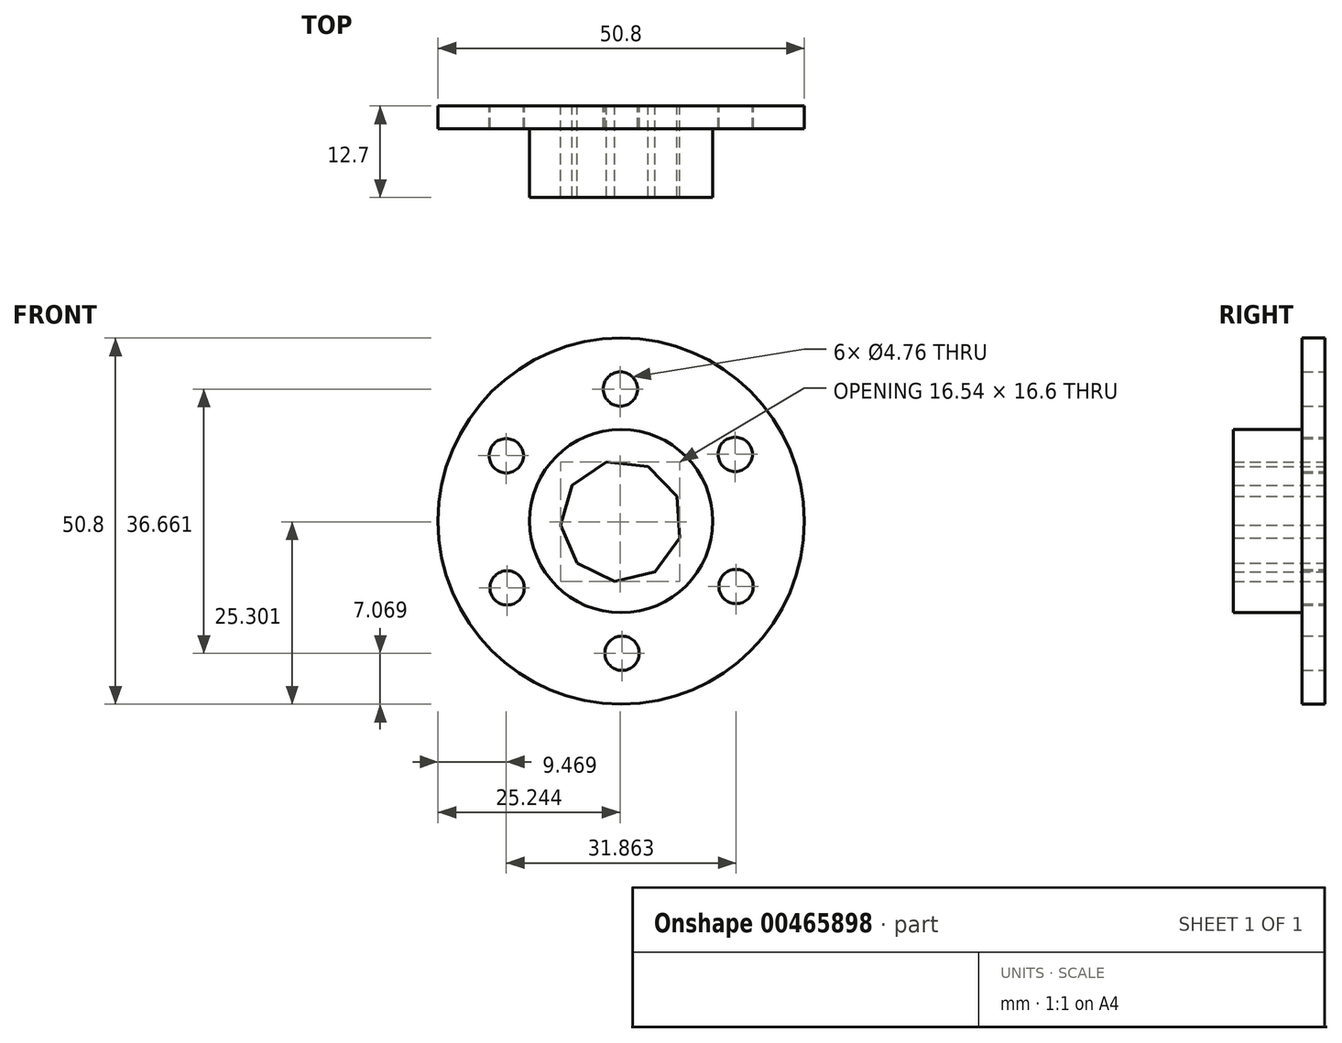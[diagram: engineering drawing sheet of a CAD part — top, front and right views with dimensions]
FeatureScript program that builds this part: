
annotation { "Feature Type Name" : "Feature", "Feature Type Description" : "" }
export const myFeature = defineFeature(function(context is Context, id is Id, definition is map)
    precondition{}
    {
        {
            var Q0;
            Q0=qCreatedBy(makeId("Front.planeOp"),FACE);
            var sketch = newSketch(context, id + "F0", { "sketchPlane" : qUnion([Q0])});
            skCircle(sketch, "E0", {"center": v(0, 0) * mm, "radius": 25.4 * mm});
            skCircle(sketch, "E1", {"center": v(0, 0) * mm, "radius": 12.7 * mm});
            skCircle(sketch, "E2", {"center": v(0, 0) * mm, "radius": 7.94 * mm});
            skSolve(sketch);
        }
        {
            var Q0;
            Q0=makeQuery(id+"F0.imprint","IMPRINT",FACE,{"disambiguationData":[TD([[makeQuery(id+"F0.imprint","IMPRINT",EDGE,{"derivedFrom":sQuery(id+"F0.wireOp",EDGE,"E0")}),1.0]])]});
            extrude(context, id + "F1", {"entities" : qUnion([Q0]), "depth" : 3.17 * mm});
        }
        {
            var Q0;
            Q0=qCreatedBy(makeId("Front.planeOp"),FACE);
            var sketch = newSketch(context, id + "F2", { "sketchPlane" : qUnion([Q0])});
            skCircle(sketch, "E3", {"center": v(0, 0) * mm, "radius": 12.7 * mm});
            skSolve(sketch);
        }
        {
            var Q0;
            Q0=makeQuery(id+"F2.imprint","IMPRINT",FACE,{"disambiguationData":[TD([[makeQuery(id+"F2.imprint","IMPRINT",EDGE,{"derivedFrom":sQuery(id+"F2.wireOp",EDGE,"E3")}),1.0]])]});
            extrude(context, id + "F3", {"entities" : qUnion([Q0]), "operationType" : NewBodyOperationType.ADD, "depth" : 12.7 * mm});
        }
        {
            var Q0;
            Q0=qCreatedBy(makeId("Front.planeOp"),FACE);
            var sketch = newSketch(context, id + "F4", { "sketchPlane" : qUnion([Q0])});
            skCircle(sketch, "E4", {"center": v(0, 0) * mm, "radius": 7.94 * mm});
            skSolve(sketch);
        }
        {
            var Q0;
            Q0 = qSketchRegion(id + "F4", true);
            extrude(context, id + "F5", {"entities" : qUnion([Q0]), "operationType" : NewBodyOperationType.REMOVE, "oppositeDirection" : true, "depth" : -76.2 * mm});
        }
        {
            var Q0;
            Q0=qCreatedBy(makeId("Front.planeOp"),FACE);
            var sketch = newSketch(context, id + "F6", { "sketchPlane" : qUnion([Q0])});
            skCircle(sketch, "E5", {"center": v(0, 0) * mm, "radius": 15.88 * mm});
            skCircle(sketch, "E6.cCircle", {"center": v(0, 0) * mm, "radius": 15.88 * mm, "construction": true});
            skLineSegment(sketch, "E6.0", {"start": v(-15.93, 9.07) * mm, "end": v(-0.11, 18.33) * mm});
            skLineSegment(sketch, "E6.1", {"start": v(-0.11, 18.33) * mm, "end": v(15.82, 9.26) * mm});
            skLineSegment(sketch, "E6.2", {"start": v(15.82, 9.26) * mm, "end": v(15.93, -9.07) * mm});
            skLineSegment(sketch, "E6.3", {"start": v(15.93, -9.07) * mm, "end": v(0.11, -18.33) * mm});
            skLineSegment(sketch, "E6.4", {"start": v(0.11, -18.33) * mm, "end": v(-15.82, -9.26) * mm});
            skLineSegment(sketch, "E6.5", {"start": v(-15.82, -9.26) * mm, "end": v(-15.93, 9.07) * mm});
            skPoint(sketch, "E6.0.midPoint", {"position": v(-8.02, 13.7) * mm});
            skCircle(sketch, "E7", {"center": v(-0.11, 18.33) * mm, "radius": 2.38 * mm});
            skCircle(sketch, "E8", {"center": v(-15.93, 9.07) * mm, "radius": 2.38 * mm});
            skCircle(sketch, "E9", {"center": v(-15.82, -9.26) * mm, "radius": 2.38 * mm});
            skCircle(sketch, "E10", {"center": v(0.11, -18.33) * mm, "radius": 2.38 * mm});
            skCircle(sketch, "E11", {"center": v(15.93, -9.07) * mm, "radius": 2.38 * mm});
            skCircle(sketch, "E12", {"center": v(15.82, 9.26) * mm, "radius": 2.38 * mm});
            skSolve(sketch);
        }
        {
            var Q0;
            {var subQ0=sQuery(id+"F6.wireOp",EDGE,"E6.1");var subQ1=sQuery(id+"F6.wireOp",EDGE,"E6.0");var subQ2=makeQuery(id+"F6.imprint","INTERSECT",VERTEX,{"derivedFrom":[subQ1,subQ0]});Q0=makeQuery(id+"F6.imprint","IMPRINT",FACE,{"disambiguationData":[TD([[makeQuery(id+"F6.imprint","IMPRINT",EDGE,{"disambiguationData":[TD([[subQ2,1.0]])],"derivedFrom":subQ1}),1.0]])]});}
            var Q1;
            {var subQ0=sQuery(id+"F6.wireOp",EDGE,"E6.1");var subQ1=sQuery(id+"F6.wireOp",EDGE,"E6.0");var subQ2=makeQuery(id+"F6.imprint","INTERSECT",VERTEX,{"derivedFrom":[subQ1,subQ0]});Q1=makeQuery(id+"F6.imprint","IMPRINT",FACE,{"disambiguationData":[TD([[makeQuery(id+"F6.imprint","IMPRINT",EDGE,{"disambiguationData":[TD([[subQ2,1.0]])],"derivedFrom":subQ1}),-1.0]])]});}
            var Q2;
            {var subQ0=sQuery(id+"F6.wireOp",EDGE,"E6.5");var subQ1=sQuery(id+"F6.wireOp",EDGE,"E6.0");var subQ2=makeQuery(id+"F6.imprint","INTERSECT",VERTEX,{"derivedFrom":[subQ1,subQ0]});Q2=makeQuery(id+"F6.imprint","IMPRINT",FACE,{"disambiguationData":[TD([[makeQuery(id+"F6.imprint","IMPRINT",EDGE,{"disambiguationData":[TD([[subQ2,-1.0]])],"derivedFrom":subQ1}),1.0]])]});}
            var Q3;
            {var subQ0=sQuery(id+"F6.wireOp",EDGE,"E6.5");var subQ1=sQuery(id+"F6.wireOp",EDGE,"E6.0");var subQ2=makeQuery(id+"F6.imprint","INTERSECT",VERTEX,{"derivedFrom":[subQ1,subQ0]});Q3=makeQuery(id+"F6.imprint","IMPRINT",FACE,{"disambiguationData":[TD([[makeQuery(id+"F6.imprint","IMPRINT",EDGE,{"disambiguationData":[TD([[subQ2,-1.0]])],"derivedFrom":subQ1}),-1.0]])]});}
            var Q4;
            {var subQ0=sQuery(id+"F6.wireOp",EDGE,"E6.2");var subQ1=sQuery(id+"F6.wireOp",EDGE,"E6.1");var subQ2=makeQuery(id+"F6.imprint","INTERSECT",VERTEX,{"derivedFrom":[subQ1,subQ0]});Q4=makeQuery(id+"F6.imprint","IMPRINT",FACE,{"disambiguationData":[TD([[makeQuery(id+"F6.imprint","IMPRINT",EDGE,{"disambiguationData":[TD([[subQ2,1.0]])],"derivedFrom":subQ1}),1.0]])]});}
            var Q5;
            {var subQ0=sQuery(id+"F6.wireOp",EDGE,"E6.2");var subQ1=sQuery(id+"F6.wireOp",EDGE,"E6.1");var subQ2=makeQuery(id+"F6.imprint","INTERSECT",VERTEX,{"derivedFrom":[subQ1,subQ0]});Q5=makeQuery(id+"F6.imprint","IMPRINT",FACE,{"disambiguationData":[TD([[makeQuery(id+"F6.imprint","IMPRINT",EDGE,{"disambiguationData":[TD([[subQ2,1.0]])],"derivedFrom":subQ1}),-1.0]])]});}
            var Q6;
            {var subQ0=sQuery(id+"F6.wireOp",EDGE,"E6.3");var subQ1=sQuery(id+"F6.wireOp",EDGE,"E6.2");var subQ2=makeQuery(id+"F6.imprint","INTERSECT",VERTEX,{"derivedFrom":[subQ1,subQ0]});Q6=makeQuery(id+"F6.imprint","IMPRINT",FACE,{"disambiguationData":[TD([[makeQuery(id+"F6.imprint","IMPRINT",EDGE,{"disambiguationData":[TD([[subQ2,1.0]])],"derivedFrom":subQ1}),1.0]])]});}
            var Q7;
            {var subQ0=sQuery(id+"F6.wireOp",EDGE,"E6.3");var subQ1=sQuery(id+"F6.wireOp",EDGE,"E6.2");var subQ2=makeQuery(id+"F6.imprint","INTERSECT",VERTEX,{"derivedFrom":[subQ1,subQ0]});Q7=makeQuery(id+"F6.imprint","IMPRINT",FACE,{"disambiguationData":[TD([[makeQuery(id+"F6.imprint","IMPRINT",EDGE,{"disambiguationData":[TD([[subQ2,1.0]])],"derivedFrom":subQ1}),-1.0]])]});}
            var Q8;
            {var subQ0=sQuery(id+"F6.wireOp",EDGE,"E6.4");var subQ1=sQuery(id+"F6.wireOp",EDGE,"E6.3");var subQ2=makeQuery(id+"F6.imprint","INTERSECT",VERTEX,{"derivedFrom":[subQ1,subQ0]});Q8=makeQuery(id+"F6.imprint","IMPRINT",FACE,{"disambiguationData":[TD([[makeQuery(id+"F6.imprint","IMPRINT",EDGE,{"disambiguationData":[TD([[subQ2,1.0]])],"derivedFrom":subQ1}),1.0]])]});}
            var Q9;
            {var subQ0=sQuery(id+"F6.wireOp",EDGE,"E6.4");var subQ1=sQuery(id+"F6.wireOp",EDGE,"E6.3");var subQ2=makeQuery(id+"F6.imprint","INTERSECT",VERTEX,{"derivedFrom":[subQ1,subQ0]});Q9=makeQuery(id+"F6.imprint","IMPRINT",FACE,{"disambiguationData":[TD([[makeQuery(id+"F6.imprint","IMPRINT",EDGE,{"disambiguationData":[TD([[subQ2,1.0]])],"derivedFrom":subQ1}),-1.0]])]});}
            var Q10;
            {var subQ0=sQuery(id+"F6.wireOp",EDGE,"E6.5");var subQ1=sQuery(id+"F6.wireOp",EDGE,"E6.4");var subQ2=makeQuery(id+"F6.imprint","INTERSECT",VERTEX,{"derivedFrom":[subQ1,subQ0]});Q10=makeQuery(id+"F6.imprint","IMPRINT",FACE,{"disambiguationData":[TD([[makeQuery(id+"F6.imprint","IMPRINT",EDGE,{"disambiguationData":[TD([[subQ2,1.0]])],"derivedFrom":subQ1}),1.0]])]});}
            var Q11;
            {var subQ0=sQuery(id+"F6.wireOp",EDGE,"E6.5");var subQ1=sQuery(id+"F6.wireOp",EDGE,"E6.4");var subQ2=makeQuery(id+"F6.imprint","INTERSECT",VERTEX,{"derivedFrom":[subQ1,subQ0]});Q11=makeQuery(id+"F6.imprint","IMPRINT",FACE,{"disambiguationData":[TD([[makeQuery(id+"F6.imprint","IMPRINT",EDGE,{"disambiguationData":[TD([[subQ2,1.0]])],"derivedFrom":subQ1}),-1.0]])]});}
            extrude(context, id + "F7", {"entities" : qUnion([Q0, Q1, Q2, Q3, Q4, Q5, Q6, Q7, Q8, Q9, Q10, Q11]), "operationType" : NewBodyOperationType.REMOVE, "oppositeDirection" : true, "depth" : -25.4 * mm});
        }
        {
            var Q0;
            Q0=qCreatedBy(makeId("Front.planeOp"),FACE);
            var sketch = newSketch(context, id + "F8", { "sketchPlane" : qUnion([Q0])});
            skCircle(sketch, "E13", {"center": v(0, 0) * mm, "radius": 7.94 * mm});
            skCircle(sketch, "E14.cCircle", {"center": v(0, 0) * mm, "radius": 7.94 * mm, "construction": true});
            skLineSegment(sketch, "E14.0", {"start": v(-6.82, 4.98) * mm, "end": v(-2.03, 8.2) * mm});
            skLineSegment(sketch, "E14.1", {"start": v(-2.03, 8.2) * mm, "end": v(3.72, 7.58) * mm});
            skLineSegment(sketch, "E14.2", {"start": v(3.72, 7.58) * mm, "end": v(7.72, 3.42) * mm});
            skLineSegment(sketch, "E14.3", {"start": v(7.72, 3.42) * mm, "end": v(8.11, -2.34) * mm});
            skLineSegment(sketch, "E14.4", {"start": v(8.11, -2.34) * mm, "end": v(4.7, -7.01) * mm});
            skLineSegment(sketch, "E14.5", {"start": v(4.7, -7.01) * mm, "end": v(-0.9, -8.4) * mm});
            skLineSegment(sketch, "E14.6", {"start": v(-0.9, -8.4) * mm, "end": v(-6.09, -5.86) * mm});
            skLineSegment(sketch, "E14.7", {"start": v(-6.09, -5.86) * mm, "end": v(-8.43, -0.57) * mm});
            skLineSegment(sketch, "E14.8", {"start": v(-8.43, -0.57) * mm, "end": v(-6.82, 4.98) * mm});
            skPoint(sketch, "E14.0.midPoint", {"position": v(-4.43, 6.59) * mm});
            skSolve(sketch);
        }
        {
            var Q0;
            {var subQ0=sQuery(id+"F8.wireOp",EDGE,"E14.1");var subQ1=sQuery(id+"F8.wireOp",EDGE,"E13");var subQ2=makeQuery(id+"F8.imprint","INTERSECT",VERTEX,{"derivedFrom":[subQ1,subQ0]});Q0=makeQuery(id+"F8.imprint","IMPRINT",FACE,{"disambiguationData":[TD([[makeQuery(id+"F8.imprint","IMPRINT",EDGE,{"disambiguationData":[TD([[subQ2,-1.0]])],"derivedFrom":subQ1}),-1.0]])]});}
            var Q1;
            {var subQ0=sQuery(id+"F8.wireOp",EDGE,"E14.0");var subQ1=sQuery(id+"F8.wireOp",EDGE,"E13");var subQ2=makeQuery(id+"F8.imprint","INTERSECT",VERTEX,{"derivedFrom":[subQ1,subQ0]});Q1=makeQuery(id+"F8.imprint","IMPRINT",FACE,{"disambiguationData":[TD([[makeQuery(id+"F8.imprint","IMPRINT",EDGE,{"disambiguationData":[TD([[subQ2,-1.0]])],"derivedFrom":subQ1}),-1.0]])]});}
            var Q2;
            {var subQ0=sQuery(id+"F8.wireOp",EDGE,"E14.2");var subQ1=sQuery(id+"F8.wireOp",EDGE,"E13");var subQ2=makeQuery(id+"F8.imprint","INTERSECT",VERTEX,{"derivedFrom":[subQ1,subQ0]});Q2=makeQuery(id+"F8.imprint","IMPRINT",FACE,{"disambiguationData":[TD([[makeQuery(id+"F8.imprint","IMPRINT",EDGE,{"disambiguationData":[TD([[subQ2,-1.0]])],"derivedFrom":subQ1}),-1.0]])]});}
            var Q3;
            {var subQ0=sQuery(id+"F8.wireOp",EDGE,"E14.2");var subQ1=sQuery(id+"F8.wireOp",EDGE,"E13");var subQ2=makeQuery(id+"F8.imprint","INTERSECT",VERTEX,{"derivedFrom":[subQ1,subQ0]});Q3=makeQuery(id+"F8.imprint","IMPRINT",FACE,{"disambiguationData":[TD([[makeQuery(id+"F8.imprint","IMPRINT",EDGE,{"disambiguationData":[TD([[subQ2,1.0]])],"derivedFrom":subQ1}),-1.0]])]});}
            var Q4;
            {var subQ0=sQuery(id+"F8.wireOp",EDGE,"E14.6");var subQ1=sQuery(id+"F8.wireOp",EDGE,"E13");var subQ2=makeQuery(id+"F8.imprint","INTERSECT",VERTEX,{"derivedFrom":[subQ1,subQ0]});Q4=makeQuery(id+"F8.imprint","IMPRINT",FACE,{"disambiguationData":[TD([[makeQuery(id+"F8.imprint","IMPRINT",EDGE,{"disambiguationData":[TD([[subQ2,-1.0]])],"derivedFrom":subQ1}),-1.0]])]});}
            var Q5;
            {var subQ0=sQuery(id+"F8.wireOp",EDGE,"E14.5");var subQ1=sQuery(id+"F8.wireOp",EDGE,"E13");var subQ2=makeQuery(id+"F8.imprint","INTERSECT",VERTEX,{"derivedFrom":[subQ1,subQ0]});Q5=makeQuery(id+"F8.imprint","IMPRINT",FACE,{"disambiguationData":[TD([[makeQuery(id+"F8.imprint","IMPRINT",EDGE,{"disambiguationData":[TD([[subQ2,-1.0]])],"derivedFrom":subQ1}),-1.0]])]});}
            var Q6;
            {var subQ0=sQuery(id+"F8.wireOp",EDGE,"E14.8");var subQ1=sQuery(id+"F8.wireOp",EDGE,"E13");var subQ2=makeQuery(id+"F8.imprint","INTERSECT",VERTEX,{"derivedFrom":[subQ1,subQ0]});Q6=makeQuery(id+"F8.imprint","IMPRINT",FACE,{"disambiguationData":[TD([[makeQuery(id+"F8.imprint","IMPRINT",EDGE,{"disambiguationData":[TD([[subQ2,-1.0]])],"derivedFrom":subQ1}),-1.0]])]});}
            var Q7;
            {var subQ0=sQuery(id+"F8.wireOp",EDGE,"E14.7");var subQ1=sQuery(id+"F8.wireOp",EDGE,"E13");var subQ2=makeQuery(id+"F8.imprint","INTERSECT",VERTEX,{"derivedFrom":[subQ1,subQ0]});Q7=makeQuery(id+"F8.imprint","IMPRINT",FACE,{"disambiguationData":[TD([[makeQuery(id+"F8.imprint","IMPRINT",EDGE,{"disambiguationData":[TD([[subQ2,-1.0]])],"derivedFrom":subQ1}),-1.0]])]});}
            var Q8;
            {var subQ0=sQuery(id+"F8.wireOp",EDGE,"E14.3");var subQ1=sQuery(id+"F8.wireOp",EDGE,"E13");var subQ2=makeQuery(id+"F8.imprint","INTERSECT",VERTEX,{"derivedFrom":[subQ1,subQ0]});Q8=makeQuery(id+"F8.imprint","IMPRINT",FACE,{"disambiguationData":[TD([[makeQuery(id+"F8.imprint","IMPRINT",EDGE,{"disambiguationData":[TD([[subQ2,1.0]])],"derivedFrom":subQ1}),-1.0]])]});}
            extrude(context, id + "F9", {"entities" : qUnion([Q0, Q1, Q2, Q3, Q4, Q5, Q6, Q7, Q8]), "operationType" : NewBodyOperationType.REMOVE, "oppositeDirection" : true, "depth" : -50.8 * mm});
        }
    });
